# Revit family: Foundation-Barrier-Stego-Crete_Claw_Tape
name_source: partatom
category: Specialty Equipment
units: mm (PartAtom-declared; Revit-internal decimal feet)

## family parameters
Cut with Voids When Loaded = No
Host = Face
OmniClass Number = 23.25.05.21
OmniClass Title = Special Foundations
Part Type = Normal
Room Calculation Point = No
Round Connector Dimension = Use Diameter
Shared = No

## types (2) — shared parameters
Brand url = http://www.stegoindustries.com
Date of publishing = 8/16/2017
Default Elevation = 0' - 0"
Description = Stego Crete Claw Tape is a multi-layered tape that is used to seal Stego®  Wrap Vapor Barrier to the perimeter of the slab while the concrete is placed. Stego Crete Claw Tape allows wet concrete to cast into the textured top surface to form a mechanical bond/ seal.  Stego Crete Claw Tape is composed of polyethylene film, aperture film, and an acrylic pressure sensitive adhesive.  Stego Crete Claw Tape is available in both six-inch wide and three-inch wide rolls.
Design country = United States
Edition number = 1
Height = 1' - 7"
Installation instructions = https://www.stegoindustries.com
Low Emitting Material = Yes
Manufacturer = Stego Industries, LLC
Manufacturer country = United States
Manufacturer name = Stego Industries, LLC
Masterformat 2014 Code = 07 26 00
Masterformat 2014 Description = Vapor Retarders
Material main = Polyethylene
Material secondary = Acrylic
Max Length Note = Stego® Crete Claw® Tape is available in rolls of 180'.
Model = Stego® Crete Claw® Tape
Nominal height = 0' - 0"
Nominal width = 0' - 0"
Product Documentation Link = https://www.stegoindustries.com
Product Guid = 0717d0b4-04e0-4d62-bec9-3d9bfa1c79a4
Product Page URL = https://www.stegoindustries.com
Product SKU = stego003
Product certification = https://www.stegoindustries.com
Product data url = https://bimobject.com
Product family = Thermal and Moisture Protective Products
Product group = Stego Crete Claw Tape
Product url = https://www.stegoindustries.com
QR code = https://bimobject.com
Technical description = Double-sided, pressure-sensitive vapor-proofing specialty tape.
Thickness = 0' - 0 1/16"
URL = https://www.stegoindustries.com
Weight Net (Kg) = 0
Youtube clip = https://www.youtube.com

## per-type parameters (varying)
| type | BIMobject category | Crete Claw Depth | Stego Crete Claw |
| Stego® Crete Claw® 6" Wide | Waterproofing & Membranes | 0' - 6" | <By Category> |
| Stego® Crete Claw® 3" Wide | Waterproofing & Membranes
Waterproofing & Membranes | 0' - 3" | Stego® Crete Claw® Tape |

## geometry (parser evidence)
native form markers: Sweep x2
no freeform markers — native parametric forms only
